# Revit family: DBLTD_TheSenatorGroup_OffcStrg_Play_MediaUnit_US
name_source: partatom
category: Furniture
revit_build: Autodesk Revit 2018 (Build: 20170223_1515(x64)
units: mm (PartAtom-declared; Revit-internal decimal feet)

## family parameters
Always vertical = Yes
Cut with Voids When Loaded = No
Room Calculation Point = No
Shared = Yes
Work Plane-Based = No

## types (1)
- Media Unit 60"(w) x 18"(d) x 70"(h)
    AssetType = Movable
    BIMObjectName = TheSenatorGroup_OfficeStorage_Play_MediaUnit
    Category = Pr_40_30_78_57:Office storage units
    Cost = 0 $
    Description = Play Media Unit With Storage
    DimensionsHeight = 70"
    DimensionsPlanSize = 60" x 18"
    DurationUnit = year
    Finish = HD Highland Oak, BH Beech, MP Maple, WH White, AT Autumn. WK Winter Oak, SO Strata Oak, MC Mocha, HW Hacienda White, DN Denim, LY Clay, LS Lemon Sorbet, LG Light Grey, CW Carini Walnut
    FramesColour = Black, White, Totally Orange, Traffic Yellow, Anthracite, Pistachio
    IfcExportAs = IfcFurnitureType
    IfcExportType = STORAGE
    Keynote = Pr_40_50_21_60
    Manufacturer = The Senator Group
    ManufacturerName = The Senator Group
    ManufacturerURL = https://www.thesenatorgroup.com
    Material = Metal, MFC
    Model = PYP70-60-MU
    ModelNumber = PYP70-60-MU
    ModelReference = 60"(w) x 18"(d) x70"(h)
    NBSDescription = Office storage
    NBSReference = 45-35-80/360
    Name = TheSenatorGroup_OfficeStorage_Play_MediaUnit
    NominalDepth = 18 "
    NominalHeight = 70 "
    NominalLength = 60 "
    NominalWidth = 60 "
    OmniClassCode = 22-12 51 19
    OmniClassTitle = Storage
    OmniClassVersion = Table 22 2012-05-16
    ProductInformation = https://www.thesenatorgroup.com
    Size = L 18" x  W 60" x  H 70"
    URL = https://www.thesenatorgroup.com
    Uniclass2015Code = Pr_40_30_78_57
    Uniclass2015Title = Office storage units
    Uniclass2015Version = Products v1.9
    Version = 1
    WarrantyDescription = Senator warrants that its manufactured products are free from manufacturing defects - in materials or workmanship - for a period of ten (10) years on Senator Seating ranges; and fifteen (15) years on Senator Desking ranges
    WarrantyDurationLabor = 15
    WarrantyDurationParts = 15
    WarrantyDurationUnit = Years
    WarrantyGuarantorLabor = 15
    WarrantyGuarantorParts = 15

## geometry (parser evidence)
native form markers: Sweep x2
no freeform markers — native parametric forms only
